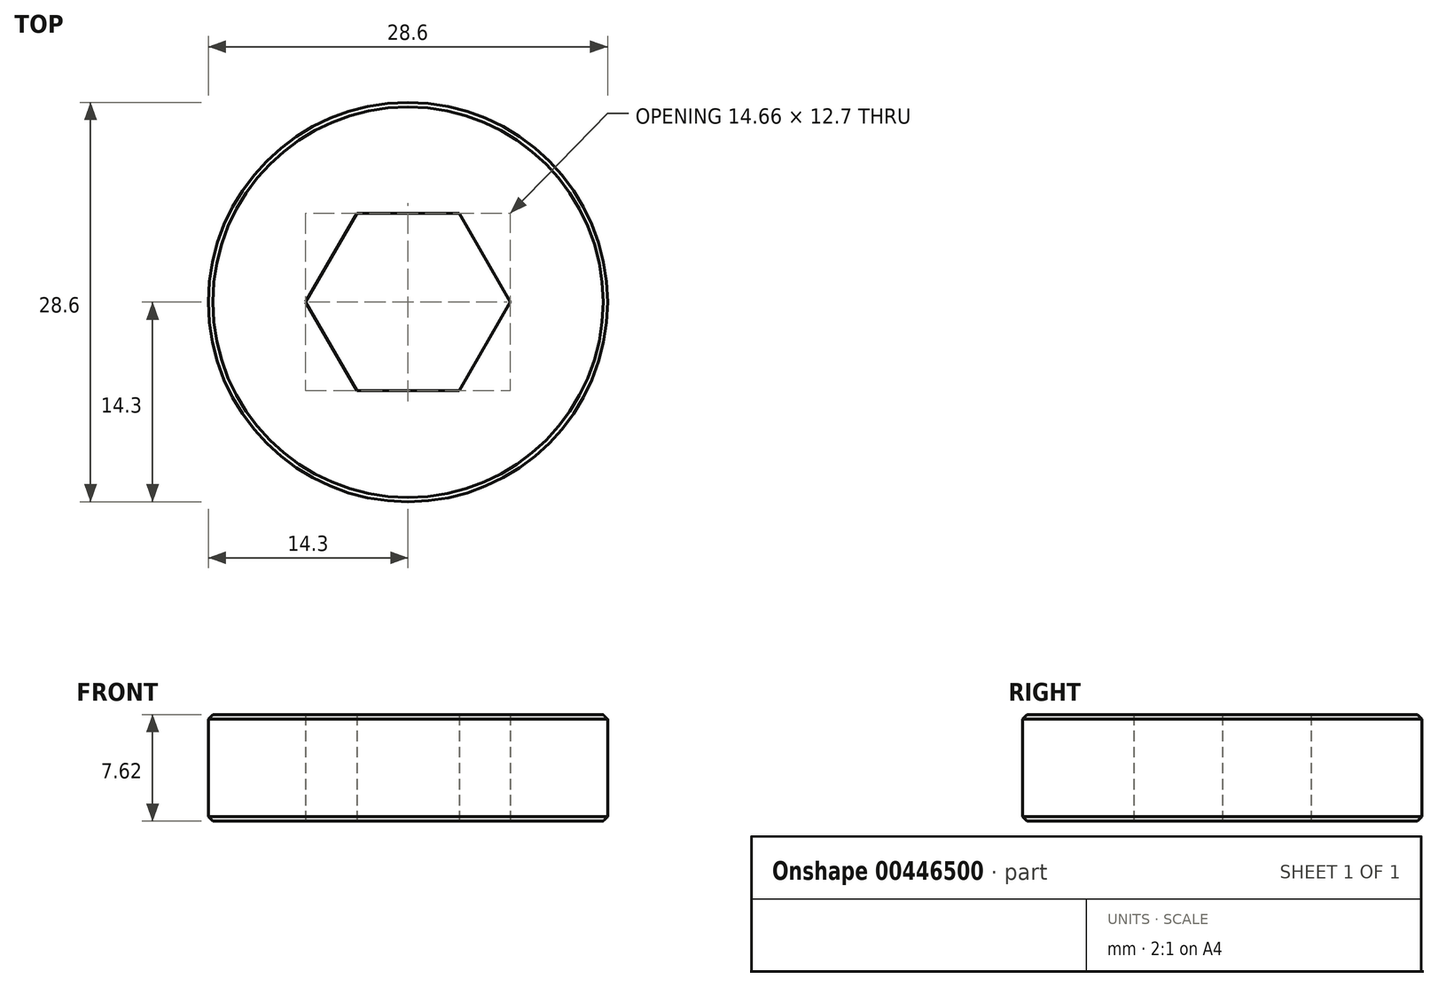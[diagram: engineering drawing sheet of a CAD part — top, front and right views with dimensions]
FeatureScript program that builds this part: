
annotation { "Feature Type Name" : "Feature", "Feature Type Description" : "" }
export const myFeature = defineFeature(function(context is Context, id is Id, definition is map)
    precondition{}
    {
        {
            var Q0;
            Q0=qCreatedBy(makeId("Top.planeOp"),FACE);
            var sketch = newSketch(context, id + "F0", { "sketchPlane" : qUnion([Q0])});
            skCircle(sketch, "E0", {"center": v(0, 0) * mm, "radius": 14.3 * mm});
            skCircle(sketch, "E1.cCircle", {"center": v(0, 0) * mm, "radius": 6.35 * mm, "construction": true});
            skLineSegment(sketch, "E1.0", {"start": v(3.67, 6.35) * mm, "end": v(7.33, 0) * mm});
            skLineSegment(sketch, "E1.1", {"start": v(7.33, 0) * mm, "end": v(3.67, -6.35) * mm});
            skLineSegment(sketch, "E1.2", {"start": v(3.67, -6.35) * mm, "end": v(-3.67, -6.35) * mm});
            skLineSegment(sketch, "E1.3", {"start": v(-3.67, -6.35) * mm, "end": v(-7.33, 0) * mm});
            skLineSegment(sketch, "E1.4", {"start": v(-7.33, 0) * mm, "end": v(-3.67, 6.35) * mm});
            skLineSegment(sketch, "E1.5", {"start": v(-3.67, 6.35) * mm, "end": v(3.67, 6.35) * mm});
            skPoint(sketch, "E1.0.midPoint", {"position": v(5.5, 3.18) * mm});
            skSolve(sketch);
        }
        {
            var Q0;
            Q0=makeQuery(id+"F0.imprint","IMPRINT",FACE,{"disambiguationData":[TD([[makeQuery(id+"F0.imprint","IMPRINT",EDGE,{"derivedFrom":sQuery(id+"F0.wireOp",EDGE,"E0")}),1.0]])]});
            extrude(context, id + "F1", {"entities" : qUnion([Q0]), "depth" : 7.62 * mm, "symmetric" : true});
        }
        {
            var Q0;
            Q0=makeQuery(id+"F1.opExtrude","CAP_EDGE",EDGE,{"disambiguationData":[OSD([sQuery(id+"F0.wireOp",EDGE,"E0")])],"isStart":false});
            var Q1;
            Q1=makeQuery(id+"F1.opExtrude","CAP_EDGE",EDGE,{"disambiguationData":[OSD([sQuery(id+"F0.wireOp",EDGE,"E0")])],"isStart":true});
            chamfer(context, id + "F2", {"entities" : qUnion([Q0, Q1]), "width" : 0.32 * mm, "tangentPropagation" : true});
        }
    });
